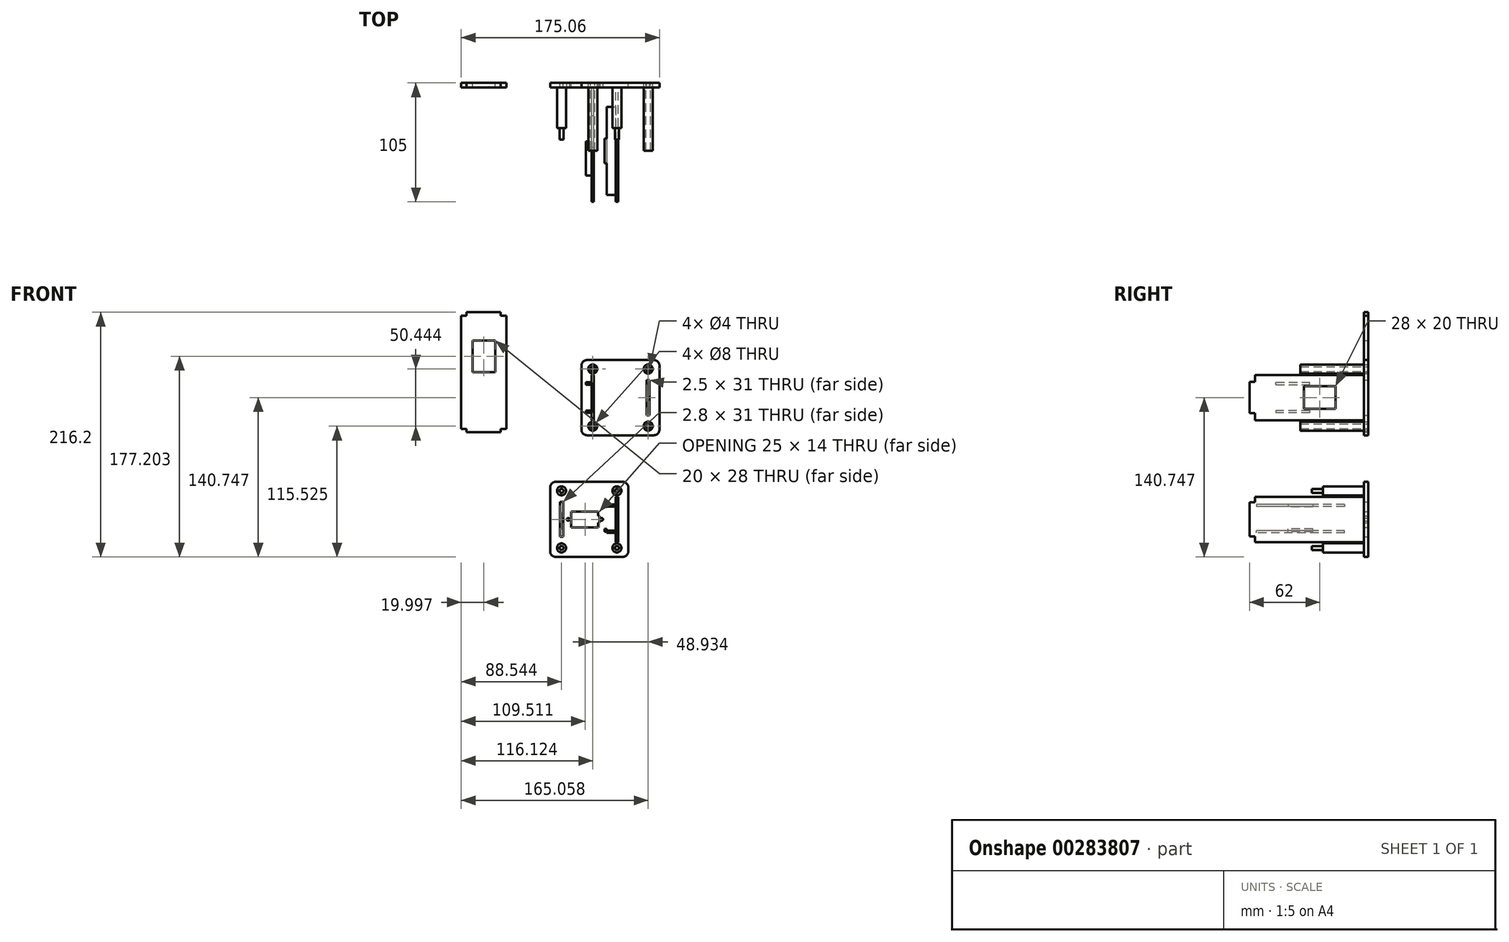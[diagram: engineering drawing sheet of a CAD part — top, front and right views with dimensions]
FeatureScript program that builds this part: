
annotation { "Feature Type Name" : "Feature", "Feature Type Description" : "" }
export const myFeature = defineFeature(function(context is Context, id is Id, definition is map)
    precondition{}
    {
        {
            var Q0;
            Q0=qCreatedBy(makeId("Front.planeOp"),FACE);
            var sketch = newSketch(context, id + "F0", { "sketchPlane" : qUnion([Q0])});
            skLineSegment(sketch, "E0.bottom", {"start": v(-69.08, 91.05) * mm, "end": v(-128.02, 91.05) * mm});
            skLineSegment(sketch, "E0.top", {"start": v(-69.08, 24.6) * mm, "end": v(-128.02, 24.6) * mm});
            skLineSegment(sketch, "E0.left", {"start": v(-64.08, 86.05) * mm, "end": v(-64.08, 29.6) * mm});
            skLineSegment(sketch, "E0.right", {"start": v(-133.02, 86.05) * mm, "end": v(-133.02, 29.6) * mm});
            skPoint(sketch, "E1", {"position": v(-98.55, 91.05) * mm});
            skPoint(sketch, "E2", {"position": v(-64.08, 57.83) * mm});
            skPoint(sketch, "E3", {"position": v(-133.02, 57.83) * mm});
            skPoint(sketch, "E4", {"position": v(-98.55, 24.6) * mm});
            skCircle(sketch, "E5", {"center": v(-123.02, 83.05) * mm, "radius": 4 * mm});
            skCircle(sketch, "E6", {"center": v(-74.08, 83.05) * mm, "radius": 4 * mm});
            skCircle(sketch, "E7", {"center": v(-74.08, 32.6) * mm, "radius": 4 * mm});
            skCircle(sketch, "E8", {"center": v(-123.02, 32.6) * mm, "radius": 4 * mm});
            skPoint(sketch, "E9.visualSharp", {"position": v(-133.02, 91.05) * mm});
            skArc(sketch, "E9.filletArc", {"start": v(-128.02, 91.05) * mm, "mid": v(-131.55, 89.58) * mm, "end": v(-133.02, 86.05) * mm});
            skPoint(sketch, "E10.visualSharp", {"position": v(-64.08, 91.05) * mm});
            skArc(sketch, "E10.filletArc", {"start": v(-64.08, 86.05) * mm, "mid": v(-65.55, 89.58) * mm, "end": v(-69.08, 91.05) * mm});
            skPoint(sketch, "E11.visualSharp", {"position": v(-64.08, 24.6) * mm});
            skArc(sketch, "E11.filletArc", {"start": v(-69.08, 24.6) * mm, "mid": v(-65.55, 26.07) * mm, "end": v(-64.08, 29.6) * mm});
            skPoint(sketch, "E12.visualSharp", {"position": v(-133.02, 24.6) * mm});
            skArc(sketch, "E12.filletArc", {"start": v(-133.02, 29.6) * mm, "mid": v(-131.55, 26.07) * mm, "end": v(-128.02, 24.6) * mm});
            skLineSegment(sketch, "E13.bottom", {"start": v(-75.33, 73.33) * mm, "end": v(-72.83, 73.33) * mm});
            skLineSegment(sketch, "E13.top", {"start": v(-75.33, 42.33) * mm, "end": v(-72.83, 42.33) * mm});
            skLineSegment(sketch, "E13.left", {"start": v(-75.33, 73.33) * mm, "end": v(-75.33, 42.33) * mm});
            skLineSegment(sketch, "E13.right", {"start": v(-72.83, 73.33) * mm, "end": v(-72.83, 42.33) * mm});
            skPoint(sketch, "E13.middle", {"position": v(-74.08, 57.83) * mm});
            skCircle(sketch, "E14", {"center": v(-123.02, 32.6) * mm, "radius": 2 * mm});
            skCircle(sketch, "E15", {"center": v(-74.08, 32.6) * mm, "radius": 2 * mm});
            skCircle(sketch, "E16", {"center": v(-123.02, 83.05) * mm, "radius": 2 * mm});
            skCircle(sketch, "E17", {"center": v(-74.08, 83.05) * mm, "radius": 2 * mm});
            skLineSegment(sketch, "E18.bottom", {"start": v(-122.02, 37.83) * mm, "end": v(-124.02, 37.83) * mm});
            skLineSegment(sketch, "E18.top", {"start": v(-122.02, 77.83) * mm, "end": v(-124.02, 77.83) * mm});
            skLineSegment(sketch, "E18.left", {"start": v(-122.02, 37.83) * mm, "end": v(-122.02, 77.83) * mm});
            skLineSegment(sketch, "E18.right", {"start": v(-124.02, 37.83) * mm, "end": v(-124.02, 77.83) * mm});
            skPoint(sketch, "E18.middle", {"position": v(-123.02, 57.83) * mm});
            skLineSegment(sketch, "E19.bottom", {"start": v(-96.66, -16.48) * mm, "end": v(-155.6, -16.48) * mm});
            skLineSegment(sketch, "E19.top", {"start": v(-96.66, -82.92) * mm, "end": v(-155.6, -82.92) * mm});
            skLineSegment(sketch, "E19.left", {"start": v(-91.66, -21.48) * mm, "end": v(-91.66, -77.92) * mm});
            skLineSegment(sketch, "E19.right", {"start": v(-160.6, -21.48) * mm, "end": v(-160.6, -77.92) * mm});
            skLineSegment(sketch, "E20.bottom", {"start": v(-118.13, -42.7) * mm, "end": v(-142.13, -42.7) * mm});
            skLineSegment(sketch, "E20.top", {"start": v(-118.13, -56.7) * mm, "end": v(-142.13, -56.7) * mm});
            skLineSegment(sketch, "E20.left", {"start": v(-118.13, -42.7) * mm, "end": v(-118.13, -56.7) * mm});
            skLineSegment(sketch, "E20.right", {"start": v(-142.13, -42.7) * mm, "end": v(-142.13, -56.7) * mm});
            skLineSegment(sketch, "E21.bottom", {"start": v(-117.13, -46.7) * mm, "end": v(-118.13, -46.7) * mm});
            skLineSegment(sketch, "E21.top", {"start": v(-117.13, -52.7) * mm, "end": v(-118.13, -52.7) * mm});
            skLineSegment(sketch, "E21.left", {"start": v(-117.13, -46.7) * mm, "end": v(-117.13, -52.7) * mm});
            skLineSegment(sketch, "E21.right", {"start": v(-118.13, -46.7) * mm, "end": v(-118.13, -52.7) * mm});
            skCircle(sketch, "E22", {"center": v(-115.13, -49.7) * mm, "radius": 1.25 * mm});
            skCircle(sketch, "E23", {"center": v(-144.66, -49.7) * mm, "radius": 1.25 * mm});
            skPoint(sketch, "E24", {"position": v(-142.13, -49.7) * mm});
            skPoint(sketch, "E25", {"position": v(-117.13, -49.7) * mm});
            skPoint(sketch, "E26", {"position": v(-118.13, -49.7) * mm});
            skPoint(sketch, "E27", {"position": v(-126.13, -16.48) * mm});
            skPoint(sketch, "E28", {"position": v(-91.66, -49.7) * mm});
            skPoint(sketch, "E29", {"position": v(-160.6, -49.7) * mm});
            skPoint(sketch, "E30", {"position": v(-126.13, -82.92) * mm});
            skLineSegment(sketch, "E31", {"start": v(-60.76, -49.7) * mm, "end": v(-190.13, -49.7) * mm, "construction": true});
            skPoint(sketch, "E32", {"position": v(-126.13, -42.7) * mm});
            skCircle(sketch, "E33", {"center": v(-150.6, -24.48) * mm, "radius": 4 * mm});
            skCircle(sketch, "E34", {"center": v(-101.66, -24.48) * mm, "radius": 4 * mm});
            skCircle(sketch, "E35", {"center": v(-101.66, -74.92) * mm, "radius": 4 * mm});
            skCircle(sketch, "E36", {"center": v(-150.6, -74.92) * mm, "radius": 4 * mm});
            skPoint(sketch, "E37.visualSharp", {"position": v(-160.6, -16.48) * mm});
            skArc(sketch, "E37.filletArc", {"start": v(-155.6, -16.48) * mm, "mid": v(-159.13, -17.94) * mm, "end": v(-160.6, -21.48) * mm});
            skPoint(sketch, "E38.visualSharp", {"position": v(-91.66, -16.48) * mm});
            skArc(sketch, "E38.filletArc", {"start": v(-91.66, -21.48) * mm, "mid": v(-93.13, -17.94) * mm, "end": v(-96.66, -16.48) * mm});
            skPoint(sketch, "E39.visualSharp", {"position": v(-91.66, -82.92) * mm});
            skArc(sketch, "E39.filletArc", {"start": v(-96.66, -82.92) * mm, "mid": v(-93.13, -81.46) * mm, "end": v(-91.66, -77.92) * mm});
            skPoint(sketch, "E40.visualSharp", {"position": v(-160.6, -82.92) * mm});
            skArc(sketch, "E40.filletArc", {"start": v(-160.6, -77.92) * mm, "mid": v(-159.13, -81.46) * mm, "end": v(-155.6, -82.92) * mm});
            skLineSegment(sketch, "E41.bottom", {"start": v(-152, -34.2) * mm, "end": v(-149.2, -34.2) * mm});
            skLineSegment(sketch, "E41.top", {"start": v(-152, -65.2) * mm, "end": v(-149.2, -65.2) * mm});
            skLineSegment(sketch, "E41.left", {"start": v(-152, -34.2) * mm, "end": v(-152, -65.2) * mm});
            skLineSegment(sketch, "E41.right", {"start": v(-149.2, -34.2) * mm, "end": v(-149.2, -65.2) * mm});
            skPoint(sketch, "E41.middle", {"position": v(-150.6, -49.7) * mm});
            skLineSegment(sketch, "E42.bottom", {"start": v(-100.66, -69.7) * mm, "end": v(-102.66, -69.7) * mm});
            skLineSegment(sketch, "E42.top", {"start": v(-100.66, -29.7) * mm, "end": v(-102.66, -29.7) * mm});
            skLineSegment(sketch, "E42.left", {"start": v(-100.66, -69.7) * mm, "end": v(-100.66, -29.7) * mm});
            skLineSegment(sketch, "E42.right", {"start": v(-102.66, -69.7) * mm, "end": v(-102.66, -29.7) * mm});
            skPoint(sketch, "E42.middle", {"position": v(-101.66, -49.7) * mm});
            skLineSegment(sketch, "E43.bottom", {"start": v(-199.14, 30.28) * mm, "end": v(-204.33, 30.28) * mm});
            skLineSegment(sketch, "E43.top", {"start": v(-199.14, 130.28) * mm, "end": v(-204.33, 130.28) * mm});
            skLineSegment(sketch, "E43.left", {"start": v(-199.14, 30.28) * mm, "end": v(-199.14, 130.28) * mm});
            skLineSegment(sketch, "E43.right", {"start": v(-239.14, 30.28) * mm, "end": v(-239.14, 130.28) * mm});
            skPoint(sketch, "E43.middle", {"position": v(-219.14, 80.28) * mm});
            skLineSegment(sketch, "E44.bottom", {"start": v(-204.33, 27.28) * mm, "end": v(-234.33, 27.28) * mm});
            skLineSegment(sketch, "E44.left", {"start": v(-204.33, 27.28) * mm, "end": v(-204.33, 30.28) * mm});
            skLineSegment(sketch, "E44.right", {"start": v(-234.33, 27.28) * mm, "end": v(-234.33, 30.28) * mm});
            skLineSegment(sketch, "E45.bottom", {"start": v(-204.33, 133.28) * mm, "end": v(-234.33, 133.28) * mm});
            skLineSegment(sketch, "E45.left", {"start": v(-204.33, 133.28) * mm, "end": v(-204.33, 130.28) * mm});
            skLineSegment(sketch, "E45.right", {"start": v(-234.33, 133.28) * mm, "end": v(-234.33, 130.28) * mm});
            skLineSegment(sketch, "E46.trimOffspring", {"start": v(-234.33, 130.28) * mm, "end": v(-239.14, 130.28) * mm});
            skLineSegment(sketch, "E47.trimOffspring", {"start": v(-234.33, 30.28) * mm, "end": v(-239.14, 30.28) * mm});
            skLineSegment(sketch, "E48.bottom", {"start": v(-209.14, 80.28) * mm, "end": v(-229.14, 80.28) * mm});
            skLineSegment(sketch, "E48.top", {"start": v(-209.14, 108.28) * mm, "end": v(-229.14, 108.28) * mm});
            skLineSegment(sketch, "E48.left", {"start": v(-209.14, 80.28) * mm, "end": v(-209.14, 108.28) * mm});
            skLineSegment(sketch, "E48.right", {"start": v(-229.14, 80.28) * mm, "end": v(-229.14, 108.28) * mm});
            skPoint(sketch, "E48.middle", {"position": v(-219.14, 94.28) * mm});
            skCircle(sketch, "E49", {"center": v(-150.6, -24.48) * mm, "radius": 1.75 * mm});
            skCircle(sketch, "E50", {"center": v(-101.66, -24.48) * mm, "radius": 1.75 * mm});
            skCircle(sketch, "E51", {"center": v(-101.66, -74.92) * mm, "radius": 1.75 * mm});
            skCircle(sketch, "E52", {"center": v(-150.6, -74.92) * mm, "radius": 1.75 * mm});
            skSolve(sketch);
        }
        {
            var Q0;
            Q0=makeQuery(id+"F0.imprint","IMPRINT",FACE,{"disambiguationData":[TD([[makeQuery(id+"F0.imprint","IMPRINT",EDGE,{"derivedFrom":sQuery(id+"F0.wireOp",EDGE,"E5")}),1.0]])]});
            var Q1;
            Q1=makeQuery(id+"F0.imprint","IMPRINT",FACE,{"disambiguationData":[TD([[makeQuery(id+"F0.imprint","IMPRINT",EDGE,{"derivedFrom":sQuery(id+"F0.wireOp",EDGE,"E6")}),1.0]])]});
            var Q2;
            Q2=makeQuery(id+"F0.imprint","IMPRINT",FACE,{"disambiguationData":[TD([[makeQuery(id+"F0.imprint","IMPRINT",EDGE,{"derivedFrom":sQuery(id+"F0.wireOp",EDGE,"E7")}),1.0]])]});
            var Q3;
            Q3=makeQuery(id+"F0.imprint","IMPRINT",FACE,{"disambiguationData":[TD([[makeQuery(id+"F0.imprint","IMPRINT",EDGE,{"derivedFrom":sQuery(id+"F0.wireOp",EDGE,"E8")}),1.0]])]});
            extrude(context, id + "F1", {"entities" : qUnion([Q0, Q1, Q2, Q3]), "depth" : 60 * mm});
        }
        {
            var Q0;
            {Q0=qUnion([makeQuery(id+"F0.imprint","IMPRINT",FACE,{"disambiguationData":[TD([[makeQuery(id+"F0.imprint","IMPRINT",EDGE,{"derivedFrom":sQuery(id+"F0.wireOp",EDGE,"E43.bottom")}),-1.0]])]}),makeQuery(id+"F0.imprint","IMPRINT",FACE,{"disambiguationData":[TD([[makeQuery(id+"F0.imprint","IMPRINT",EDGE,{"derivedFrom":sQuery(id+"F0.wireOp",EDGE,"E0.bottom")}),1.0]])]}),makeQuery(id+"F0.imprint","IMPRINT",FACE,{"disambiguationData":[TD([[makeQuery(id+"F0.imprint","IMPRINT",EDGE,{"derivedFrom":sQuery(id+"F0.wireOp",EDGE,"E19.bottom")}),1.0]])]})]);}
            var Q1;
            Q1=makeQuery(id+"F0.imprint","IMPRINT",FACE,{"disambiguationData":[TD([[makeQuery(id+"F0.imprint","IMPRINT",EDGE,{"derivedFrom":sQuery(id+"F0.wireOp",EDGE,"E42.bottom")}),-1.0]])]});
            var Q2;
            Q2=makeQuery(id+"F0.imprint","IMPRINT",FACE,{"disambiguationData":[TD([[makeQuery(id+"F0.imprint","IMPRINT",EDGE,{"derivedFrom":sQuery(id+"F0.wireOp",EDGE,"E34")}),1.0]])]});
            var Q3;
            Q3=makeQuery(id+"F0.imprint","IMPRINT",FACE,{"disambiguationData":[TD([[makeQuery(id+"F0.imprint","IMPRINT",EDGE,{"derivedFrom":sQuery(id+"F0.wireOp",EDGE,"E33")}),1.0]])]});
            var Q4;
            Q4=makeQuery(id+"F0.imprint","IMPRINT",FACE,{"disambiguationData":[TD([[makeQuery(id+"F0.imprint","IMPRINT",EDGE,{"derivedFrom":sQuery(id+"F0.wireOp",EDGE,"E36")}),1.0]])]});
            var Q5;
            Q5=makeQuery(id+"F0.imprint","IMPRINT",FACE,{"disambiguationData":[TD([[makeQuery(id+"F0.imprint","IMPRINT",EDGE,{"derivedFrom":sQuery(id+"F0.wireOp",EDGE,"E35")}),1.0]])]});
            extrude(context, id + "F2", {"entities" : qUnion([Q0, Q1, Q2, Q3, Q4, Q5]), "depth" : 4 * mm});
        }
        {
            var Q0;
            Q0=makeQuery(id+"F0.imprint","IMPRINT",FACE,{"disambiguationData":[TD([[makeQuery(id+"F0.imprint","IMPRINT",EDGE,{"derivedFrom":sQuery(id+"F0.wireOp",EDGE,"E18.bottom")}),-1.0]])]});
            extrude(context, id + "F3", {"entities" : qUnion([Q0]), "operationType" : NewBodyOperationType.ADD, "depth" : 100 * mm});
        }
        {
            var Q0;
            Q0=makeQuery(id+"F3.opExtrude","SWEPT_FACE",FACE,{"disambiguationData":[OSD([sQuery(id+"F0.wireOp",EDGE,"E18.right")])]});
            var sketch = newSketch(context, id + "F4", { "sketchPlane" : qUnion([Q0])});
            skLineSegment(sketch, "E53.left", {"start": v(105, 71.66) * mm, "end": v(105, 44) * mm});
            skPoint(sketch, "E53.middle", {"position": v(100, 57.83) * mm});
            skLineSegment(sketch, "E54.bottom", {"start": v(57, 47.83) * mm, "end": v(29, 47.83) * mm});
            skLineSegment(sketch, "E54.top", {"start": v(57, 67.83) * mm, "end": v(29, 67.83) * mm});
            skLineSegment(sketch, "E54.left", {"start": v(57, 47.83) * mm, "end": v(57, 67.83) * mm});
            skLineSegment(sketch, "E54.right", {"start": v(29, 47.83) * mm, "end": v(29, 67.83) * mm});
            skPoint(sketch, "E54.middle", {"position": v(43, 57.83) * mm});
            skLineSegment(sketch, "E55.bottom", {"start": v(81.7, 69.34) * mm, "end": v(51.7, 69.34) * mm});
            skLineSegment(sketch, "E55.top", {"start": v(81.7, 71.34) * mm, "end": v(51.7, 71.34) * mm});
            skLineSegment(sketch, "E55.left", {"start": v(81.7, 69.34) * mm, "end": v(81.7, 71.34) * mm});
            skLineSegment(sketch, "E55.right", {"start": v(51.7, 69.34) * mm, "end": v(51.7, 71.34) * mm});
            skPoint(sketch, "E55.middle", {"position": v(66.7, 70.34) * mm});
            skLineSegment(sketch, "E56.bottom", {"start": v(51.7, 46.34) * mm, "end": v(81.7, 46.34) * mm});
            skLineSegment(sketch, "E56.top", {"start": v(51.7, 44.34) * mm, "end": v(81.7, 44.34) * mm});
            skLineSegment(sketch, "E56.left", {"start": v(51.7, 46.34) * mm, "end": v(51.7, 44.34) * mm});
            skLineSegment(sketch, "E56.right", {"start": v(81.7, 46.34) * mm, "end": v(81.7, 44.34) * mm});
            skPoint(sketch, "E56.middle", {"position": v(66.7, 45.34) * mm});
            skLineSegment(sketch, "E57", {"start": v(105, 71.66) * mm, "end": v(100, 71.66) * mm});
            skLineSegment(sketch, "E58", {"start": v(105, 44) * mm, "end": v(100, 44) * mm});
            skLineSegment(sketch, "E59", {"start": v(66.7, 70.34) * mm, "end": v(66.7, 45.32) * mm, "construction": true});
            skPoint(sketch, "E60", {"position": v(66.7, 57.83) * mm});
            skSolve(sketch);
        }
        {
            var Q0;
            Q0=makeQuery(id+"F4.imprint","IMPRINT",FACE,{"disambiguationData":[TD([[makeQuery(id+"F4.imprint","IMPRINT",EDGE,{"derivedFrom":sQuery(id+"F4.wireOp",EDGE,"E55.bottom")}),-1.0]])]});
            var Q1;
            Q1=makeQuery(id+"F4.imprint","IMPRINT",FACE,{"disambiguationData":[TD([[makeQuery(id+"F4.imprint","IMPRINT",EDGE,{"derivedFrom":sQuery(id+"F4.wireOp",EDGE,"E56.bottom")}),-1.0]])]});
            extrude(context, id + "F5", {"entities" : qUnion([Q0, Q1]), "operationType" : NewBodyOperationType.ADD, "depth" : 5 * mm});
        }
        {
            var Q0;
            Q0=makeQuery(id+"F4.imprint","IMPRINT",FACE,{"disambiguationData":[TD([[makeQuery(id+"F4.imprint","IMPRINT",EDGE,{"derivedFrom":sQuery(id+"F4.wireOp",EDGE,"E53.left")}),-1.0]])]});
            extrude(context, id + "F6", {"entities" : qUnion([Q0]), "operationType" : NewBodyOperationType.ADD, "oppositeDirection" : true, "depth" : 2 * mm});
        }
        {
            var Q0;
            Q0=makeQuery(id+"F4.imprint","IMPRINT",FACE,{"disambiguationData":[TD([[makeQuery(id+"F4.imprint","IMPRINT",EDGE,{"derivedFrom":sQuery(id+"F4.wireOp",EDGE,"E54.bottom")}),-1.0]])]});
            extrude(context, id + "F7", {"entities" : qUnion([Q0]), "operationType" : NewBodyOperationType.REMOVE, "oppositeDirection" : true, "depth" : 2 * mm});
        }
        {
            var Q0;
            Q0=makeQuery(id+"F0.imprint","IMPRINT",FACE,{"disambiguationData":[TD([[makeQuery(id+"F0.imprint","IMPRINT",EDGE,{"derivedFrom":sQuery(id+"F0.wireOp",EDGE,"E49")}),1.0]])]});
            var Q1;
            Q1=makeQuery(id+"F0.imprint","IMPRINT",FACE,{"disambiguationData":[TD([[makeQuery(id+"F0.imprint","IMPRINT",EDGE,{"derivedFrom":sQuery(id+"F0.wireOp",EDGE,"E50")}),1.0]])]});
            var Q2;
            Q2=makeQuery(id+"F0.imprint","IMPRINT",FACE,{"disambiguationData":[TD([[makeQuery(id+"F0.imprint","IMPRINT",EDGE,{"derivedFrom":sQuery(id+"F0.wireOp",EDGE,"E51")}),1.0]])]});
            var Q3;
            Q3=makeQuery(id+"F0.imprint","IMPRINT",FACE,{"disambiguationData":[TD([[makeQuery(id+"F0.imprint","IMPRINT",EDGE,{"derivedFrom":sQuery(id+"F0.wireOp",EDGE,"E52")}),1.0]])]});
            extrude(context, id + "F8", {"entities" : qUnion([Q0, Q1, Q2, Q3]), "operationType" : NewBodyOperationType.ADD, "depth" : 50 * mm});
        }
        {
            var Q0;
            Q0=makeQuery(id+"F0.imprint","IMPRINT",FACE,{"disambiguationData":[TD([[makeQuery(id+"F0.imprint","IMPRINT",EDGE,{"derivedFrom":sQuery(id+"F0.wireOp",EDGE,"E33")}),1.0]])]});
            var Q1;
            Q1=makeQuery(id+"F0.imprint","IMPRINT",FACE,{"disambiguationData":[TD([[makeQuery(id+"F0.imprint","IMPRINT",EDGE,{"derivedFrom":sQuery(id+"F0.wireOp",EDGE,"E36")}),1.0]])]});
            var Q2;
            Q2=makeQuery(id+"F0.imprint","IMPRINT",FACE,{"disambiguationData":[TD([[makeQuery(id+"F0.imprint","IMPRINT",EDGE,{"derivedFrom":sQuery(id+"F0.wireOp",EDGE,"E35")}),1.0]])]});
            var Q3;
            Q3=makeQuery(id+"F0.imprint","IMPRINT",FACE,{"disambiguationData":[TD([[makeQuery(id+"F0.imprint","IMPRINT",EDGE,{"derivedFrom":sQuery(id+"F0.wireOp",EDGE,"E34")}),1.0]])]});
            extrude(context, id + "F9", {"entities" : qUnion([Q0, Q1, Q2, Q3]), "operationType" : NewBodyOperationType.ADD, "depth" : 40 * mm});
        }
        {
            var Q0;
            Q0=makeQuery(id+"F0.imprint","IMPRINT",FACE,{"disambiguationData":[TD([[makeQuery(id+"F0.imprint","IMPRINT",EDGE,{"derivedFrom":sQuery(id+"F0.wireOp",EDGE,"E42.bottom")}),-1.0]])]});
            extrude(context, id + "F10", {"entities" : qUnion([Q0]), "operationType" : NewBodyOperationType.ADD, "depth" : 100 * mm});
        }
        {
            var Q0;
            Q0=makeQuery(id+"F10.opExtrude","SWEPT_FACE",FACE,{"disambiguationData":[OSD([sQuery(id+"F0.wireOp",EDGE,"E42.right")])]});
            var sketch = newSketch(context, id + "F11", { "sketchPlane" : qUnion([Q0])});
            skLineSegment(sketch, "E61.bottom", {"start": v(21, -36.34) * mm, "end": v(99, -36.34) * mm});
            skLineSegment(sketch, "E61.top", {"start": v(21, -38.34) * mm, "end": v(99, -38.34) * mm});
            skLineSegment(sketch, "E61.left", {"start": v(21, -36.34) * mm, "end": v(21, -38.34) * mm});
            skLineSegment(sketch, "E61.right", {"start": v(99, -36.34) * mm, "end": v(99, -38.34) * mm});
            skPoint(sketch, "E61.middle", {"position": v(60, -37.34) * mm});
            skPoint(sketch, "E61.middle.positionSnap0", {"position": v(52, -29.7) * mm});
            skPoint(sketch, "E61.centerSnap0", {"position": v(52, -29.7) * mm});
            skLineSegment(sketch, "E62.bottom", {"start": v(21, -61.6) * mm, "end": v(99, -61.6) * mm});
            skLineSegment(sketch, "E62.top", {"start": v(21, -59.6) * mm, "end": v(99, -59.6) * mm});
            skLineSegment(sketch, "E62.left", {"start": v(21, -61.6) * mm, "end": v(21, -59.6) * mm});
            skLineSegment(sketch, "E62.right", {"start": v(99, -61.6) * mm, "end": v(99, -59.6) * mm});
            skPoint(sketch, "E62.middle", {"position": v(60, -60.6) * mm});
            skSolve(sketch);
        }
        {
            var Q0;
            Q0=makeQuery(id+"F11.imprint","IMPRINT",FACE,{"disambiguationData":[TD([[makeQuery(id+"F11.imprint","IMPRINT",EDGE,{"derivedFrom":sQuery(id+"F11.wireOp",EDGE,"E61.bottom")}),-1.0]])]});
            var Q1;
            Q1=makeQuery(id+"F11.imprint","IMPRINT",FACE,{"disambiguationData":[TD([[makeQuery(id+"F11.imprint","IMPRINT",EDGE,{"derivedFrom":sQuery(id+"F11.wireOp",EDGE,"E62.bottom")}),1.0]])]});
            extrude(context, id + "F12", {"entities" : qUnion([Q0, Q1]), "operationType" : NewBodyOperationType.ADD, "depth" : 8 * mm});
        }
        {
            var Q0;
            Q0=makeQuery(id+"F10.opExtrude","CAP_FACE",FACE,{"disambiguationData":[OSD([sQuery(id+"F0.wireOp",EDGE,"E42.bottom"),sQuery(id+"F0.wireOp",EDGE,"E42.top"),sQuery(id+"F0.wireOp",EDGE,"E42.left"),sQuery(id+"F0.wireOp",EDGE,"E42.right")])],"isStart":false});
            var sketch = newSketch(context, id + "F13", { "sketchPlane" : qUnion([Q0])});
            skLineSegment(sketch, "E63.bottom", {"start": v(-102.66, -64.7) * mm, "end": v(-100.66, -64.7) * mm});
            skLineSegment(sketch, "E63.top", {"start": v(-102.66, -34.7) * mm, "end": v(-100.66, -34.7) * mm});
            skLineSegment(sketch, "E63.left", {"start": v(-102.66, -64.7) * mm, "end": v(-102.66, -34.7) * mm});
            skLineSegment(sketch, "E63.right", {"start": v(-100.66, -64.7) * mm, "end": v(-100.66, -34.7) * mm});
            skPoint(sketch, "E64", {"position": v(-102.66, -49.7) * mm});
            skPoint(sketch, "E65", {"position": v(-100.66, -49.7) * mm});
            skSolve(sketch);
        }
        {
            var Q0;
            Q0=makeQuery(id+"F13.imprint","IMPRINT",FACE,{"disambiguationData":[TD([[makeQuery(id+"F13.imprint","IMPRINT",EDGE,{"derivedFrom":sQuery(id+"F13.wireOp",EDGE,"E63.bottom")}),1.0]])]});
            extrude(context, id + "F14", {"entities" : qUnion([Q0]), "operationType" : NewBodyOperationType.ADD, "depth" : 5 * mm});
        }
        {
            var Q0;
            Q0=makeQuery(id+"F12.opExtrude","CAP_FACE",FACE,{"disambiguationData":[OSD([sQuery(id+"F11.wireOp",EDGE,"E61.bottom"),sQuery(id+"F11.wireOp",EDGE,"E61.top"),sQuery(id+"F11.wireOp",EDGE,"E61.left"),sQuery(id+"F11.wireOp",EDGE,"E61.right")])],"isStart":false});
            var sketch = newSketch(context, id + "F15", { "sketchPlane" : qUnion([Q0])});
            skLineSegment(sketch, "E66.bottom", {"start": v(49, -36.34) * mm, "end": v(71, -36.34) * mm});
            skLineSegment(sketch, "E66.top", {"start": v(49, -38.84) * mm, "end": v(71, -38.84) * mm});
            skLineSegment(sketch, "E66.left", {"start": v(71, -36.34) * mm, "end": v(71, -38.84) * mm});
            skLineSegment(sketch, "E66.right", {"start": v(49, -36.34) * mm, "end": v(49, -38.84) * mm});
            skPoint(sketch, "E67", {"position": v(60, -38.84) * mm});
            skLineSegment(sketch, "E68.bottom", {"start": v(49, -60.6) * mm, "end": v(71, -60.6) * mm});
            skLineSegment(sketch, "E68.top", {"start": v(49, -58.1) * mm, "end": v(71, -58.1) * mm});
            skLineSegment(sketch, "E68.left", {"start": v(71, -60.6) * mm, "end": v(71, -58.1) * mm});
            skLineSegment(sketch, "E68.right", {"start": v(49, -60.6) * mm, "end": v(49, -58.1) * mm});
            skPoint(sketch, "E69", {"position": v(60, -58.1) * mm});
            skSolve(sketch);
        }
        {
            var Q0;
            {var subQ0=sQuery(id+"F15.wireOp",EDGE,"E66.bottom");Q0=makeQuery(id+"F15.imprint","IMPRINT",FACE,{"disambiguationData":[TD([[makeQuery(id+"F15.imprint","IMPRINT",EDGE,{"derivedFrom":subQ0}),-1.0]])]});}
            var Q1;
            {var subQ0=sQuery(id+"F15.wireOp",EDGE,"E66.top");Q1=makeQuery(id+"F15.imprint","IMPRINT",FACE,{"disambiguationData":[TD([[makeQuery(id+"F15.imprint","IMPRINT",EDGE,{"derivedFrom":subQ0}),1.0]])]});}
            var Q2;
            Q2=makeQuery(id+"F15.imprint","IMPRINT",FACE,{"disambiguationData":[TD([[makeQuery(id+"F15.imprint","IMPRINT",EDGE,{"derivedFrom":sQuery(id+"F15.wireOp",EDGE,"E68.bottom")}),1.0]])]});
            extrude(context, id + "F16", {"entities" : qUnion([Q0, Q1, Q2]), "operationType" : NewBodyOperationType.ADD, "depth" : 2 * mm});
        }
    });
